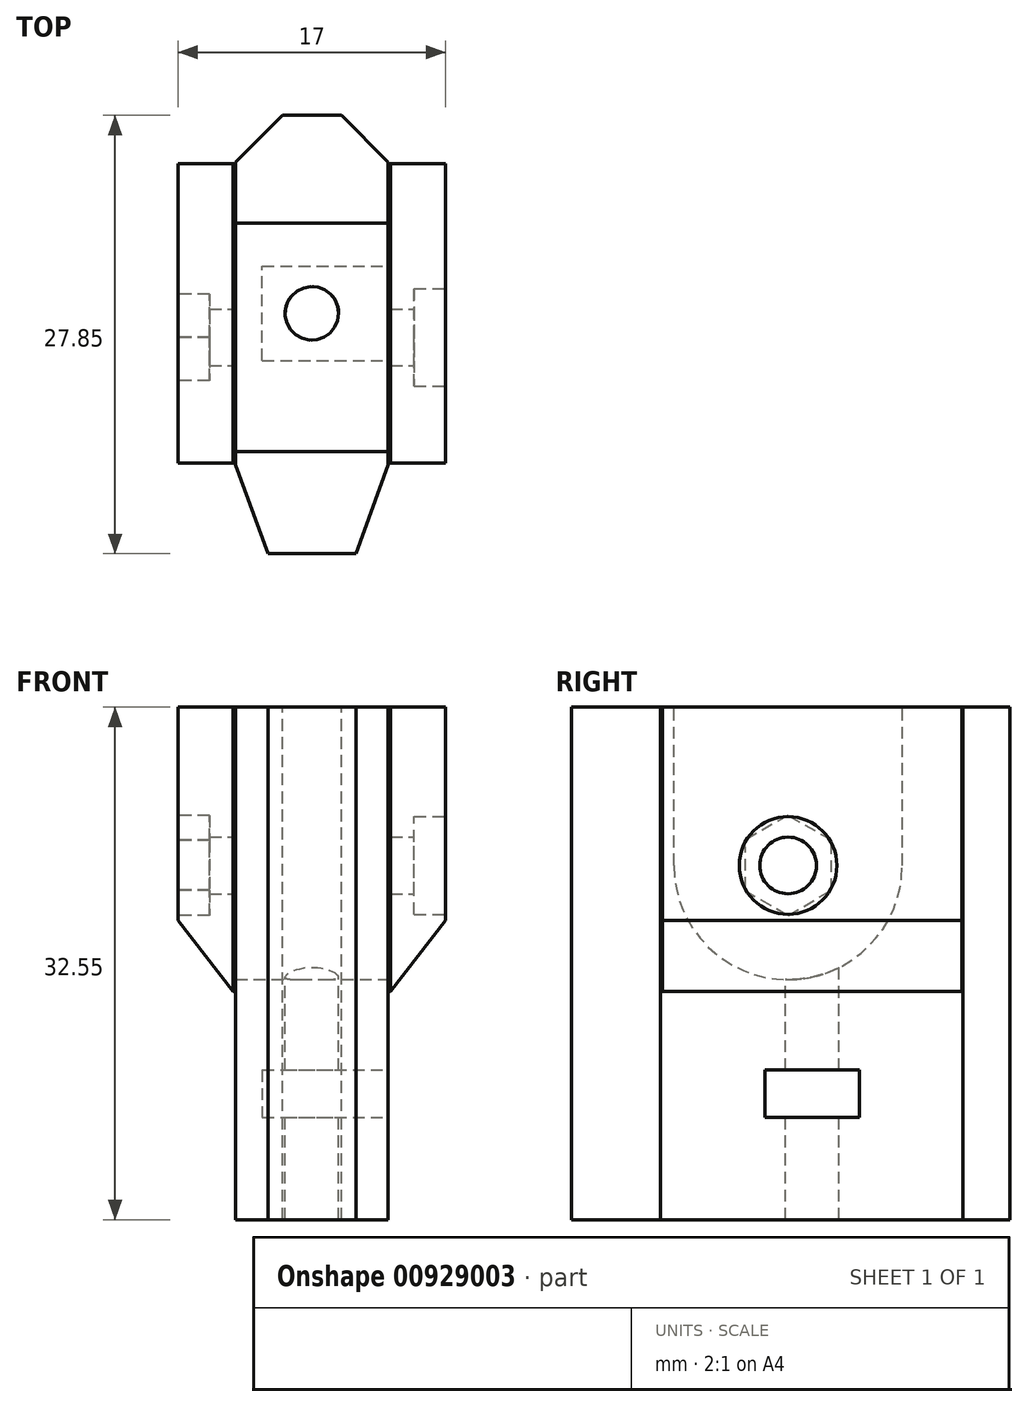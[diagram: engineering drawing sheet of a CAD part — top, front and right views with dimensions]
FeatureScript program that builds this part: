
annotation { "Feature Type Name" : "Feature", "Feature Type Description" : "" }
export const myFeature = defineFeature(function(context is Context, id is Id, definition is map)
    precondition{}
    {
        {
            var Q0;
            Q0=qCreatedBy(makeId("Top.planeOp"),FACE);
            var sketch = newSketch(context, id + "F0", { "sketchPlane" : qUnion([Q0])});
            skLineSegment(sketch, "E0", {"start": v(-25.67, 0) * mm, "end": v(37.09, 0) * mm, "construction": true});
            skLineSegment(sketch, "E1", {"start": v(0, 12.73) * mm, "end": v(-1.93, 12.73) * mm, "construction": true});
            skLineSegment(sketch, "E2", {"start": v(-1.93, 12.73) * mm, "end": v(-5, 9.66) * mm, "construction": true});
            skLineSegment(sketch, "E3", {"start": v(-5, -9.66) * mm, "end": v(-2.95, -15.27) * mm, "construction": true});
            skLineSegment(sketch, "E4", {"start": v(-2.96, -15.27) * mm, "end": v(0, -15.27) * mm, "construction": true});
            skLineSegment(sketch, "E5", {"start": v(0, -31.85) * mm, "end": v(0, 31.57) * mm, "construction": true});
            skLineSegment(sketch, "E6.1", {"start": v(-4.85, -9.63) * mm, "end": v(-2.85, -15.12) * mm});
            skLineSegment(sketch, "E6.2", {"start": v(0, 12.58) * mm, "end": v(-1.87, 12.58) * mm});
            skLineSegment(sketch, "E6.3", {"start": v(-1.87, 12.58) * mm, "end": v(-4.85, 9.6) * mm});
            skLineSegment(sketch, "E6.4", {"start": v(-4.85, 9.6) * mm, "end": v(-4.85, 0) * mm});
            skLineSegment(sketch, "E6.5", {"start": v(-4.85, 0) * mm, "end": v(-4.85, -9.63) * mm});
            skLineSegment(sketch, "E7.MirrorCS", {"start": v(0, 12.58) * mm, "end": v(1.87, 12.58) * mm});
            skLineSegment(sketch, "E8.MirrorCS", {"start": v(1.87, 12.58) * mm, "end": v(4.85, 9.6) * mm});
            skLineSegment(sketch, "E9.MirrorCS", {"start": v(4.85, 9.6) * mm, "end": v(4.85, 0) * mm});
            skLineSegment(sketch, "E10.MirrorCS", {"start": v(4.85, 0) * mm, "end": v(4.85, -9.63) * mm});
            skLineSegment(sketch, "E11.MirrorCS", {"start": v(4.85, -9.63) * mm, "end": v(2.85, -15.12) * mm});
            skCircle(sketch, "E12", {"center": v(0, 0) * mm, "radius": 1.7 * mm});
            skLineSegment(sketch, "E13", {"start": v(-5, 9.5) * mm, "end": v(-8.5, 9.5) * mm});
            skLineSegment(sketch, "E14", {"start": v(-8.5, 9.5) * mm, "end": v(-8.5, 0) * mm});
            skLineSegment(sketch, "E15", {"start": v(-5, 9.5) * mm, "end": v(-5, 0) * mm});
            skLineSegment(sketch, "E16.MirrorCS", {"start": v(-8.5, -9.5) * mm, "end": v(-8.5, 0) * mm});
            skLineSegment(sketch, "E17.MirrorCS", {"start": v(-5, -9.5) * mm, "end": v(-8.5, -9.5) * mm});
            skLineSegment(sketch, "E18.MirrorCS", {"start": v(-5, -9.5) * mm, "end": v(-5, 0) * mm});
            skLineSegment(sketch, "E19.MirrorCS", {"start": v(5, 9.5) * mm, "end": v(8.5, 9.5) * mm});
            skLineSegment(sketch, "E20.MirrorCS", {"start": v(8.5, 9.5) * mm, "end": v(8.5, 0) * mm});
            skLineSegment(sketch, "E21.MirrorCS", {"start": v(8.5, -9.5) * mm, "end": v(8.5, 0) * mm});
            skLineSegment(sketch, "E22.MirrorCS", {"start": v(5, -9.5) * mm, "end": v(8.5, -9.5) * mm});
            skLineSegment(sketch, "E23.MirrorCS", {"start": v(5, -9.5) * mm, "end": v(5, 0) * mm});
            skLineSegment(sketch, "E24.MirrorCS", {"start": v(5, 9.5) * mm, "end": v(5, 0) * mm});
            skPoint(sketch, "E25", {"position": v(0, 12.73) * mm});
            skLineSegment(sketch, "E26", {"start": v(-2.85, -15.12) * mm, "end": v(-2.8, -15.27) * mm});
            skLineSegment(sketch, "E27.MirrorCS", {"start": v(2.85, -15.12) * mm, "end": v(2.8, -15.27) * mm});
            skLineSegment(sketch, "E28", {"start": v(-2.8, -15.27) * mm, "end": v(2.8, -15.27) * mm});
            skSolve(sketch);
        }
        {
            var Q0;
            Q0=makeQuery(id+"F0.imprint","IMPRINT",FACE,{"disambiguationData":[TD([[makeQuery(id+"F0.imprint","IMPRINT",EDGE,{"derivedFrom":sQuery(id+"F0.wireOp",EDGE,"E13")}),1.0]])]});
            var Q1;
            Q1=makeQuery(id+"F0.imprint","IMPRINT",FACE,{"disambiguationData":[TD([[makeQuery(id+"F0.imprint","IMPRINT",EDGE,{"derivedFrom":sQuery(id+"F0.wireOp",EDGE,"E19.MirrorCS")}),-1.0]])]});
            extrude(context, id + "F1", {"entities" : qUnion([Q0, Q1]), "depth" : 18.05 * mm, "offsetDistance" : 25 * mm});
        }
        {
            var Q0;
            Q0=makeQuery(id+"F0.imprint","IMPRINT",FACE,{"disambiguationData":[TD([[makeQuery(id+"F0.imprint","IMPRINT",EDGE,{"derivedFrom":sQuery(id+"F0.wireOp",EDGE,"E6.1")}),1.0]])]});
            extrude(context, id + "F2", {"entities" : qUnion([Q0]), "oppositeDirection" : true, "depth" : 14.5 * mm, "offsetDistance" : 25 * mm, "hasSecondDirection" : true, "secondDirectionOppositeDirection" : false, "secondDirectionDepth" : 18.05 * mm});
        }
        {
            var Q0;
            Q0=makeQuery(id+"F1.opExtrude","SWEPT_FACE",FACE,{"disambiguationData":[OSD([sQuery(id+"F0.wireOp",EDGE,"E20.MirrorCS"),sQuery(id+"F0.wireOp",EDGE,"E21.MirrorCS")])]});
            var sketch = newSketch(context, id + "F3", { "sketchPlane" : qUnion([Q0])});
            skLineSegment(sketch, "E29", {"start": v(-1.52, 43.26) * mm, "end": v(-1.52, -42.48) * mm, "construction": true});
            skLineSegment(sketch, "E30", {"start": v(28.04, 8) * mm, "end": v(-29.93, 8) * mm, "construction": true});
            skPoint(sketch, "E31", {"position": v(-1.52, 8) * mm});
            skCircle(sketch, "E32", {"center": v(-1.52, 8) * mm, "radius": 6.5 * mm, "construction": true});
            skSolve(sketch);
        }
        {
            var Q0;
            Q0=sQuery(id+"F3.wireOp",VERTEX,"E31");
            var Q1;
            Q1=makeQuery(id+"F1.opExtrude","SWEPT_BODY",BODY,{"disambiguationData":[OSD([sQuery(id+"F0.wireOp",EDGE,"E19.MirrorCS"),sQuery(id+"F0.wireOp",EDGE,"E20.MirrorCS"),sQuery(id+"F0.wireOp",EDGE,"E21.MirrorCS"),sQuery(id+"F0.wireOp",EDGE,"E22.MirrorCS"),sQuery(id+"F0.wireOp",EDGE,"E23.MirrorCS"),sQuery(id+"F0.wireOp",EDGE,"E24.MirrorCS")])]});
            var Q2;
            Q2=makeQuery(id+"F1.opExtrude","SWEPT_BODY",BODY,{"disambiguationData":[OSD([sQuery(id+"F0.wireOp",EDGE,"E13"),sQuery(id+"F0.wireOp",EDGE,"E14"),sQuery(id+"F0.wireOp",EDGE,"E15"),sQuery(id+"F0.wireOp",EDGE,"E16.MirrorCS"),sQuery(id+"F0.wireOp",EDGE,"E17.MirrorCS"),sQuery(id+"F0.wireOp",EDGE,"E18.MirrorCS")])]});
            hole(context, id + "F4", {"style" : HoleStyle.C_BORE, "endStyle" : HoleEndStyle.THROUGH, "holeDiameter" : 3.6 * mm, "cBoreDiameter" : 6.2 * mm, "cBoreDepth" : 2 * mm, "majorDiameter" : 5 * mm, "isTappedThrough" : true, "tappedDepth" : 12 * mm, "tapClearance" : 3, "startFromSketch" : true, "locations" : qUnion([Q0]), "scope" : qUnion([Q1, Q2])});
        }
        {
            var Q0;
            Q0=makeQuery(id+"F1.opExtrude","CAP_EDGE",EDGE,{"disambiguationData":[OSD([sQuery(id+"F0.wireOp",EDGE,"E14"),sQuery(id+"F0.wireOp",EDGE,"E16.MirrorCS")])],"isStart":true});
            var Q1;
            Q1=makeQuery(id+"F1.opExtrude","CAP_EDGE",EDGE,{"disambiguationData":[OSD([sQuery(id+"F0.wireOp",EDGE,"E20.MirrorCS"),sQuery(id+"F0.wireOp",EDGE,"E21.MirrorCS")])],"isStart":true});
            chamfer(context, id + "F5", {"entities" : qUnion([Q0, Q1]), "chamferType" : ChamferType.TWO_OFFSETS, "width1" : 4.5 * mm, "oppositeDirection" : false, "width2" : 3.5 * mm, "tangentPropagation" : true});
        }
        {
            var Q0;
            Q0=makeQuery(id+"F1.opExtrude","SWEPT_FACE",FACE,{"disambiguationData":[OSD([sQuery(id+"F0.wireOp",EDGE,"E14"),sQuery(id+"F0.wireOp",EDGE,"E16.MirrorCS")])]});
            var sketch = newSketch(context, id + "F6", { "sketchPlane" : qUnion([Q0])});
            skCircle(sketch, "E33.cCircle", {"center": v(1.52, 8) * mm, "radius": 2.75 * mm, "construction": true});
            skLineSegment(sketch, "E33.0", {"start": v(1.54, 11.18) * mm, "end": v(4.28, 9.57) * mm});
            skLineSegment(sketch, "E33.1", {"start": v(4.28, 9.57) * mm, "end": v(4.27, 6.4) * mm});
            skLineSegment(sketch, "E33.2", {"start": v(4.27, 6.4) * mm, "end": v(1.5, 4.82) * mm});
            skLineSegment(sketch, "E33.3", {"start": v(1.5, 4.82) * mm, "end": v(-1.23, 6.43) * mm});
            skLineSegment(sketch, "E33.4", {"start": v(-1.23, 6.43) * mm, "end": v(-1.22, 9.6) * mm});
            skLineSegment(sketch, "E33.5", {"start": v(-1.22, 9.6) * mm, "end": v(1.54, 11.18) * mm});
            skPoint(sketch, "E33.0.midPoint", {"position": v(2.91, 10.37) * mm});
            skSolve(sketch);
        }
        {
            var Q0;
            Q0=makeQuery(id+"F6.imprint","IMPRINT",FACE,{"disambiguationData":[TD([[makeQuery(id+"F6.imprint","IMPRINT",EDGE,{"derivedFrom":sQuery(id+"F6.wireOp",EDGE,"E33.0")}),-1.0]])]});
            extrude(context, id + "F7", {"entities" : qUnion([Q0]), "operationType" : NewBodyOperationType.REMOVE, "oppositeDirection" : true, "depth" : 2 * mm, "offsetDistance" : 25 * mm});
        }
        {
            var Q0;
            Q0=makeQuery(id+"F2.opExtrude","SWEPT_FACE",FACE,{"disambiguationData":[OSD([sQuery(id+"F0.wireOp",EDGE,"E9.MirrorCS"),sQuery(id+"F0.wireOp",EDGE,"E10.MirrorCS")])]});
            var sketch = newSketch(context, id + "F8", { "sketchPlane" : qUnion([Q0])});
            skLineSegment(sketch, "E34", {"start": v(0, -5) * mm, "end": v(3, -5) * mm});
            skLineSegment(sketch, "E35", {"start": v(3, -5) * mm, "end": v(3, -8) * mm});
            skLineSegment(sketch, "E36", {"start": v(3, -8) * mm, "end": v(0, -8) * mm});
            skLineSegment(sketch, "E37.MirrorCS", {"start": v(0, -5) * mm, "end": v(-3, -5) * mm});
            skLineSegment(sketch, "E38.MirrorCS", {"start": v(-3, -5) * mm, "end": v(-3, -8) * mm});
            skLineSegment(sketch, "E39.MirrorCS", {"start": v(-3, -8) * mm, "end": v(0, -8) * mm});
            skArc(sketch, "E40", {"start": v(-8.77, 8) * mm, "mid": v(-1.52, 0.75) * mm, "end": v(5.73, 8) * mm});
            skLineSegment(sketch, "E41", {"start": v(5.73, 8) * mm, "end": v(5.73, 18.05) * mm});
            skLineSegment(sketch, "E42", {"start": v(-8.77, 8) * mm, "end": v(-8.77, 18.05) * mm});
            skLineSegment(sketch, "E43", {"start": v(5.73, 18.05) * mm, "end": v(-8.77, 18.05) * mm});
            skLineSegment(sketch, "E44", {"start": v(-9.5, 18.05) * mm, "end": v(-8.77, 18.05) * mm});
            skLineSegment(sketch, "E45", {"start": v(9.5, 18.05) * mm, "end": v(5.73, 18.05) * mm});
            skSolve(sketch);
        }
        {
            var Q0;
            Q0=makeQuery(id+"F8.imprint","IMPRINT",FACE,{"disambiguationData":[TD([[makeQuery(id+"F8.imprint","IMPRINT",EDGE,{"derivedFrom":sQuery(id+"F8.wireOp",EDGE,"E34")}),-1.0]])]});
            extrude(context, id + "F9", {"entities" : qUnion([Q0]), "operationType" : NewBodyOperationType.REMOVE, "oppositeDirection" : true, "depth" : 8 * mm, "offsetDistance" : 25 * mm});
        }
        {
            var Q0;
            Q0=makeQuery(id+"F8.imprint","IMPRINT",FACE,{"disambiguationData":[TD([[makeQuery(id+"F8.imprint","IMPRINT",EDGE,{"derivedFrom":sQuery(id+"F8.wireOp",EDGE,"E40")}),1.0]])]});
            var Q1;
            Q1=makeQuery(id+"F2.opExtrude","SWEPT_BODY",BODY,{"disambiguationData":[OSD([sQuery(id+"F0.wireOp",EDGE,"E6.0"),sQuery(id+"F0.wireOp",EDGE,"E6.1"),sQuery(id+"F0.wireOp",EDGE,"E6.2"),sQuery(id+"F0.wireOp",EDGE,"E6.3"),sQuery(id+"F0.wireOp",EDGE,"E6.4"),sQuery(id+"F0.wireOp",EDGE,"E6.5"),sQuery(id+"F0.wireOp",EDGE,"E7.MirrorCS"),sQuery(id+"F0.wireOp",EDGE,"E8.MirrorCS"),sQuery(id+"F0.wireOp",EDGE,"E9.MirrorCS"),sQuery(id+"F0.wireOp",EDGE,"E10.MirrorCS"),sQuery(id+"F0.wireOp",EDGE,"E11.MirrorCS"),sQuery(id+"F0.wireOp",EDGE,"37bbc0db-56eb-4107-8967-c16d97b151150.MirrorCS"),sQuery(id+"F0.wireOp",EDGE,"E12")])]});
            extrude(context, id + "F10", {"entities" : qUnion([Q0]), "operationType" : NewBodyOperationType.REMOVE, "endBound" : BoundingType.UP_TO_BODY, "oppositeDirection" : true, "depth" : 10 * mm, "endBoundEntityBody" : qUnion([Q1]), "offsetDistance" : 25 * mm});
        }
        {
            var Q0;
            Q0=makeQuery(id+"F1.opExtrude","SWEPT_FACE",FACE,{"disambiguationData":[OSD([sQuery(id+"F0.wireOp",EDGE,"E15"),sQuery(id+"F0.wireOp",EDGE,"E18.MirrorCS")])]});
            var Q1;
            Q1=makeQuery(id+"F2.opExtrude","SWEPT_FACE",FACE,{"disambiguationData":[OSD([sQuery(id+"F0.wireOp",EDGE,"E6.4"),sQuery(id+"F0.wireOp",EDGE,"E6.5")])]});
            var Q2;
            Q2=makeQuery(id+"F1.opExtrude","SWEPT_FACE",FACE,{"disambiguationData":[OSD([sQuery(id+"F0.wireOp",EDGE,"E23.MirrorCS"),sQuery(id+"F0.wireOp",EDGE,"E24.MirrorCS")])]});
            extrude(context, id + "F11", {"entities" : qUnion([Q0]), "endBound" : BoundingType.UP_TO_SURFACE, "depth" : 25 * mm, "endBoundEntityFace" : qUnion([Q1]), "offsetDistance" : 25 * mm});
        }
        {
            var Q0;
            Q0=makeQuery(id+"F1.opExtrude","SWEPT_FACE",FACE,{"disambiguationData":[OSD([sQuery(id+"F0.wireOp",EDGE,"E23.MirrorCS"),sQuery(id+"F0.wireOp",EDGE,"E24.MirrorCS")])]});
            var Q1;
            Q1=makeQuery(id+"F2.opExtrude","SWEPT_FACE",FACE,{"disambiguationData":[OSD([sQuery(id+"F0.wireOp",EDGE,"E9.MirrorCS"),sQuery(id+"F0.wireOp",EDGE,"E10.MirrorCS")])]});
            extrude(context, id + "F12", {"entities" : qUnion([Q0]), "endBound" : BoundingType.UP_TO_SURFACE, "depth" : 25 * mm, "endBoundEntityFace" : qUnion([Q1]), "offsetDistance" : 25 * mm});
        }
    });
